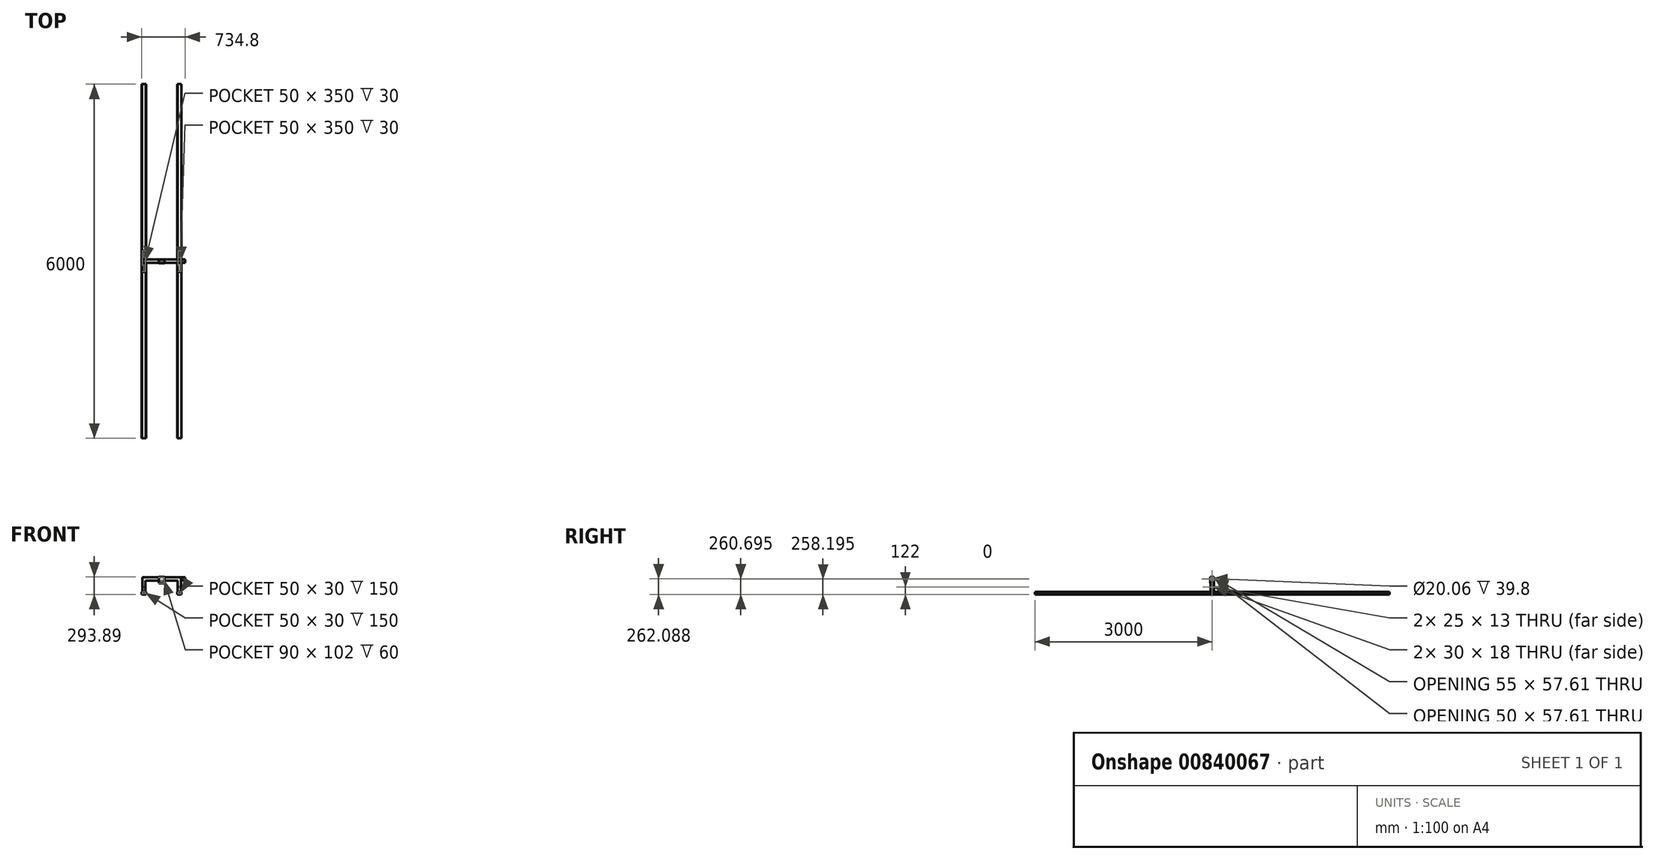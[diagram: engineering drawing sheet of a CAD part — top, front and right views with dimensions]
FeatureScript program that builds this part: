
annotation { "Feature Type Name" : "Feature", "Feature Type Description" : "" }
export const myFeature = defineFeature(function(context is Context, id is Id, definition is map)
    precondition{}
    {
        {
            var Q0;
            Q0=qCreatedBy(makeId("Top.planeOp"),FACE);
            var sketch = newSketch(context, id + "F0", { "sketchPlane" : qUnion([Q0])});
            skLineSegment(sketch, "E0", {"start": v(-300, 0) * mm, "end": v(300, 0) * mm});
            skLineSegment(sketch, "E1.bottom", {"start": v(-275, -25) * mm, "end": v(-325, -25) * mm});
            skLineSegment(sketch, "E1.top", {"start": v(-275, 25) * mm, "end": v(-325, 25) * mm});
            skLineSegment(sketch, "E1.left", {"start": v(-275, -25) * mm, "end": v(-275, 25) * mm});
            skLineSegment(sketch, "E1.right", {"start": v(-325, -25) * mm, "end": v(-325, 25) * mm});
            skPoint(sketch, "E1.middle", {"position": v(-300, 0) * mm});
            skLineSegment(sketch, "E2", {"start": v(0, 0) * mm, "end": v(0, 104.38) * mm, "construction": true});
            skLineSegment(sketch, "E3.MirrorCS", {"start": v(275, 25) * mm, "end": v(325, 25) * mm});
            skLineSegment(sketch, "E4.MirrorCS", {"start": v(275, -25) * mm, "end": v(275, 25) * mm});
            skLineSegment(sketch, "E5.MirrorCS", {"start": v(325, -25) * mm, "end": v(325, 25) * mm});
            skLineSegment(sketch, "E6.MirrorCS", {"start": v(275, -25) * mm, "end": v(325, -25) * mm});
            skSolve(sketch);
        }
        {
            var Q0;
            Q0 = qSketchRegion(id + "F0", true);
            extrude(context, id + "F1", {"entities" : qUnion([Q0]), "endBound" : BoundingType.SYMMETRIC, "depth" : 220 * mm, "offsetDistance" : 25 * mm});
        }
        {
            var Q0;
            Q0=makeQuery(id+"F1.opExtrude","CAP_FACE",FACE,{"disambiguationData":[OSD([sQuery(id+"F0.wireOp",EDGE,"E1.bottom"),sQuery(id+"F0.wireOp",EDGE,"E1.top"),sQuery(id+"F0.wireOp",EDGE,"E1.left"),sQuery(id+"F0.wireOp",EDGE,"E1.right")])],"isStart":false});
            var sketch = newSketch(context, id + "F2", { "sketchPlane" : qUnion([Q0])});
            skLineSegment(sketch, "E7.0.1", {"start": v(-275, 25) * mm, "end": v(-325, 25) * mm});
            skLineSegment(sketch, "E7.0.2", {"start": v(-325, 25) * mm, "end": v(-325, -25) * mm});
            skLineSegment(sketch, "E7.0.3", {"start": v(-325, -25) * mm, "end": v(-275, -25) * mm});
            skLineSegment(sketch, "E8.0.1", {"start": v(275, -25) * mm, "end": v(325, -25) * mm});
            skLineSegment(sketch, "E8.0.2", {"start": v(325, -25) * mm, "end": v(325, 25) * mm});
            skLineSegment(sketch, "E8.0.3", {"start": v(325, 25) * mm, "end": v(275, 25) * mm});
            skLineSegment(sketch, "E9", {"start": v(-275, 25) * mm, "end": v(275, 25) * mm});
            skLineSegment(sketch, "E10", {"start": v(-275, -25) * mm, "end": v(275, -25) * mm});
            skSolve(sketch);
        }
        {
            var Q0;
            Q0 = qSketchRegion(id + "F2", true);
            extrude(context, id + "F3", {"entities" : qUnion([Q0]), "operationType" : NewBodyOperationType.ADD, "depth" : 55 * mm, "offsetDistance" : 25 * mm});
        }
        {
            var Q0;
            Q0=makeQuery(id+"F1.opExtrude","SWEPT_FACE",FACE,{"disambiguationData":[OSD([sQuery(id+"F0.wireOp",EDGE,"E1.right")])]});
            var sketch = newSketch(context, id + "F4", { "sketchPlane" : qUnion([Q0])});
            skLineSegment(sketch, "E11.0.0", {"start": v(-25, -110) * mm, "end": v(25, -110) * mm});
            skLineSegment(sketch, "E11.0.1", {"start": v(25, -110) * mm, "end": v(25, 110) * mm});
            skLineSegment(sketch, "E11.0.3", {"start": v(-25, 110) * mm, "end": v(-25, -110) * mm});
            skLineSegment(sketch, "E12", {"start": v(0, 22) * mm, "end": v(0, 9) * mm});
            skLineSegment(sketch, "E13", {"start": v(0, -22) * mm, "end": v(0, -35) * mm});
            skLineSegment(sketch, "E14.bottom", {"start": v(15, 35) * mm, "end": v(-15, 35) * mm});
            skLineSegment(sketch, "E14.top", {"start": v(15, 53) * mm, "end": v(-15, 53) * mm});
            skLineSegment(sketch, "E14.left", {"start": v(15, 35) * mm, "end": v(15, 53) * mm});
            skLineSegment(sketch, "E14.right", {"start": v(-15, 35) * mm, "end": v(-15, 53) * mm});
            skPoint(sketch, "E14.middle", {"position": v(0, 44) * mm});
            skLineSegment(sketch, "E15.bottom", {"start": v(15, -9) * mm, "end": v(-15, -9) * mm});
            skLineSegment(sketch, "E15.top", {"start": v(15, 9) * mm, "end": v(-15, 9) * mm});
            skLineSegment(sketch, "E15.left", {"start": v(15, -9) * mm, "end": v(15, 9) * mm});
            skLineSegment(sketch, "E15.right", {"start": v(-15, -9) * mm, "end": v(-15, 9) * mm});
            skLineSegment(sketch, "E16.bottom", {"start": v(15, -53) * mm, "end": v(-15, -53) * mm});
            skLineSegment(sketch, "E16.top", {"start": v(15, -35) * mm, "end": v(-15, -35) * mm});
            skLineSegment(sketch, "E16.left", {"start": v(15, -53) * mm, "end": v(15, -35) * mm});
            skLineSegment(sketch, "E16.right", {"start": v(-15, -53) * mm, "end": v(-15, -35) * mm});
            skPoint(sketch, "E16.middle", {"position": v(0, -44) * mm});
            skPoint(sketch, "E17.trimOffspring.end.orphan", {"position": v(0, -110) * mm});
            skLineSegment(sketch, "E18.trimOffspring", {"start": v(0, -53) * mm, "end": v(0, -66) * mm});
            skLineSegment(sketch, "E19.trimOffspring", {"start": v(0, -9) * mm, "end": v(0, -22) * mm});
            skLineSegment(sketch, "E20.trimOffspring", {"start": v(0, -9) * mm, "end": v(0, -35) * mm});
            skLineSegment(sketch, "E21.trimOffspring", {"start": v(0, 35) * mm, "end": v(0, 22) * mm});
            skLineSegment(sketch, "E22.trimOffspring", {"start": v(0, 35) * mm, "end": v(0, 9) * mm});
            skLineSegment(sketch, "E23.0.1", {"start": v(25, -110) * mm, "end": v(25, 165) * mm});
            skLineSegment(sketch, "E23.0.2", {"start": v(25, 165) * mm, "end": v(-25, 165) * mm});
            skLineSegment(sketch, "E23.0.3", {"start": v(-25, 165) * mm, "end": v(-25, -110) * mm});
            skSolve(sketch);
        }
        {
            var Q0;
            {var subQ3=sQuery(id+"F4.wireOp",EDGE,"E15.left");Q0=makeQuery(id+"F4.imprint","IMPRINT",FACE,{"disambiguationData":[TD([[makeQuery(id+"F4.imprint","IMPRINT",EDGE,{"derivedFrom":subQ3}),1.0]])]});}
            extrude(context, id + "F5", {"entities" : qUnion([Q0]), "operationType" : NewBodyOperationType.REMOVE, "oppositeDirection" : true, "depth" : 696 * mm, "offsetDistance" : 25 * mm});
        }
        {
            var Q0;
            Q0=makeQuery(id+"F3.opExtrude","CAP_FACE",FACE,{"disambiguationData":[OSD([sQuery(id+"F2.wireOp",EDGE,"E7.0.1"),sQuery(id+"F2.wireOp",EDGE,"E7.0.2"),sQuery(id+"F2.wireOp",EDGE,"E7.0.3"),sQuery(id+"F2.wireOp",EDGE,"E8.0.1"),sQuery(id+"F2.wireOp",EDGE,"E8.0.2"),sQuery(id+"F2.wireOp",EDGE,"E8.0.3"),sQuery(id+"F2.wireOp",EDGE,"E9"),sQuery(id+"F2.wireOp",EDGE,"E10")])],"isStart":false});
            var sketch = newSketch(context, id + "F6", { "sketchPlane" : qUnion([Q0])});
            skPoint(sketch, "E24.orphan", {"position": v(-292.5, -12.5) * mm});
            skPoint(sketch, "E25.orphan", {"position": v(-247.5, 12.5) * mm});
            skPoint(sketch, "E26.left.start.orphan", {"position": v(-240.34, -12.5) * mm});
            skPoint(sketch, "E26.right.end.orphan", {"position": v(-292.5, 12.5) * mm});
            skPoint(sketch, "E27.bottom.end.orphan", {"position": v(-182.5, -12.5) * mm});
            skPoint(sketch, "E28.orphan", {"position": v(-130.34, -12.5) * mm});
            skPoint(sketch, "E27.top.end.orphan", {"position": v(-182.5, 12.5) * mm});
            skPoint(sketch, "E27.top.start.orphan", {"position": v(-137.5, 12.5) * mm});
            skPoint(sketch, "E29.top.end.orphan", {"position": v(37.5, 12.5) * mm});
            skPoint(sketch, "E29.bottom.end.orphan", {"position": v(37.5, -12.5) * mm});
            skPoint(sketch, "E30.orphan", {"position": v(82.5, -12.5) * mm});
            skPoint(sketch, "E29.left.end.orphan", {"position": v(82.5, 12.5) * mm});
            skPoint(sketch, "E31.top.end.orphan", {"position": v(197.5, 12.5) * mm});
            skPoint(sketch, "E31.bottom.end.orphan", {"position": v(197.5, -12.5) * mm});
            skPoint(sketch, "E31.bottom.start.orphan", {"position": v(242.5, -12.5) * mm});
            skPoint(sketch, "E31.left.end.orphan", {"position": v(242.5, 12.5) * mm});
            skPoint(sketch, "E32.orphan", {"position": v(-72.5, -12.5) * mm});
            skPoint(sketch, "E33.orphan", {"position": v(-27.5, -12.5) * mm});
            skPoint(sketch, "E34.top.end.orphan", {"position": v(-72.5, 12.5) * mm});
            skPoint(sketch, "E34.top.start.orphan", {"position": v(-27.5, 12.5) * mm});
            skPoint(sketch, "E35.orphan", {"position": v(325, 0) * mm});
            skPoint(sketch, "E36.orphan", {"position": v(-325, 0) * mm});
            skLineSegment(sketch, "E37", {"start": v(-325, 0) * mm, "end": v(325, 0) * mm, "construction": true});
            skLineSegment(sketch, "E38", {"start": v(-325, 0) * mm, "end": v(-195, 0) * mm});
            skLineSegment(sketch, "E39", {"start": v(-195, 0) * mm, "end": v(-65, 0) * mm});
            skLineSegment(sketch, "E40", {"start": v(-65, 0) * mm, "end": v(65, 0) * mm});
            skLineSegment(sketch, "E41", {"start": v(65, 0) * mm, "end": v(195, 0) * mm});
            skLineSegment(sketch, "E42", {"start": v(195, 0) * mm, "end": v(325, 0) * mm});
            skLineSegment(sketch, "E43.top", {"start": v(-242.5, 12.5) * mm, "end": v(-247.5, 12.5) * mm});
            skPoint(sketch, "E43.middle", {"position": v(-260, 0) * mm});
            skPoint(sketch, "E44.orphan", {"position": v(-277.5, -12.5) * mm});
            skPoint(sketch, "E43.left.start.orphan", {"position": v(-242.5, -12.5) * mm});
            skPoint(sketch, "E45.orphan", {"position": v(-277.5, 12.5) * mm});
            skLineSegment(sketch, "E46.bottom", {"start": v(22.5, -12.5) * mm, "end": v(-22.5, -12.5) * mm});
            skLineSegment(sketch, "E46.top", {"start": v(22.5, 12.5) * mm, "end": v(-22.5, 12.5) * mm});
            skLineSegment(sketch, "E46.left", {"start": v(22.5, -12.5) * mm, "end": v(22.5, 12.5) * mm});
            skLineSegment(sketch, "E46.right", {"start": v(-22.5, -12.5) * mm, "end": v(-22.5, 12.5) * mm});
            skPoint(sketch, "E46.middle", {"position": v(0, 0) * mm});
            skLineSegment(sketch, "E47", {"start": v(0, 0) * mm, "end": v(-65, 0) * mm});
            skLineSegment(sketch, "E48", {"start": v(0, 0) * mm, "end": v(-110, 0) * mm});
            skLineSegment(sketch, "E49.bottom", {"start": v(-87.5, -12.5) * mm, "end": v(-132.5, -12.5) * mm});
            skLineSegment(sketch, "E49.top", {"start": v(-87.5, 12.5) * mm, "end": v(-132.5, 12.5) * mm});
            skLineSegment(sketch, "E49.left", {"start": v(-87.5, -12.5) * mm, "end": v(-87.5, 12.5) * mm});
            skLineSegment(sketch, "E49.right", {"start": v(-132.5, -12.5) * mm, "end": v(-132.5, 12.5) * mm});
            skPoint(sketch, "E49.middle", {"position": v(-110, 0) * mm});
            skLineSegment(sketch, "E50", {"start": v(0, 0) * mm, "end": v(110, 0) * mm});
            skLineSegment(sketch, "E51.bottom", {"start": v(132.5, -12.5) * mm, "end": v(87.5, -12.5) * mm});
            skLineSegment(sketch, "E51.top", {"start": v(132.5, 12.5) * mm, "end": v(87.5, 12.5) * mm});
            skLineSegment(sketch, "E51.left", {"start": v(132.5, -12.5) * mm, "end": v(132.5, 12.5) * mm});
            skLineSegment(sketch, "E51.right", {"start": v(87.5, -12.5) * mm, "end": v(87.5, 12.5) * mm});
            skPoint(sketch, "E51.middle", {"position": v(110, 0) * mm});
            skLineSegment(sketch, "E52", {"start": v(-110, 0) * mm, "end": v(-220, 0) * mm});
            skLineSegment(sketch, "E53.bottom", {"start": v(-197.5, -12.5) * mm, "end": v(-242.5, -12.5) * mm});
            skLineSegment(sketch, "E53.top", {"start": v(-197.5, 12.5) * mm, "end": v(-242.5, 12.5) * mm});
            skLineSegment(sketch, "E53.left", {"start": v(-197.5, -12.5) * mm, "end": v(-197.5, 12.5) * mm});
            skLineSegment(sketch, "E53.right", {"start": v(-242.5, -12.5) * mm, "end": v(-242.5, 12.5) * mm});
            skPoint(sketch, "E53.middle", {"position": v(-220, 0) * mm});
            skLineSegment(sketch, "E54", {"start": v(110, 0) * mm, "end": v(220, 0) * mm});
            skPoint(sketch, "E55.middle", {"position": v(195, 0) * mm});
            skPoint(sketch, "E56.orphan", {"position": v(172.5, -12.5) * mm});
            skPoint(sketch, "E57.orphan", {"position": v(172.5, 12.5) * mm});
            skPoint(sketch, "E58.orphan", {"position": v(217.5, 12.5) * mm});
            skPoint(sketch, "E55.bottom.start.orphan", {"position": v(217.5, -12.5) * mm});
            skLineSegment(sketch, "E59.bottom", {"start": v(242.5, -12.5) * mm, "end": v(197.5, -12.5) * mm});
            skLineSegment(sketch, "E59.top", {"start": v(242.5, 12.5) * mm, "end": v(197.5, 12.5) * mm});
            skLineSegment(sketch, "E59.left", {"start": v(242.5, -12.5) * mm, "end": v(242.5, 12.5) * mm});
            skLineSegment(sketch, "E59.right", {"start": v(197.5, -12.5) * mm, "end": v(197.5, 12.5) * mm});
            skPoint(sketch, "E59.middle", {"position": v(220, 0) * mm});
            skSolve(sketch);
        }
        {
            var Q0;
            Q0=makeQuery(id+"F3.boolean.opBoolean","MERGE",FACE,{"derivedFrom":[makeQuery(id+"F1.opExtrude","SWEPT_FACE",FACE,{"disambiguationData":[OSD([sQuery(id+"F0.wireOp",EDGE,"E1.bottom")])]}),makeQuery(id+"F1.opExtrude","SWEPT_FACE",FACE,{"disambiguationData":[OSD([sQuery(id+"F0.wireOp",EDGE,"E6.MirrorCS")])]}),makeQuery(id+"F3.opExtrude","SWEPT_FACE",FACE,{"disambiguationData":[OSD([sQuery(id+"F2.wireOp",EDGE,"E7.0.3"),sQuery(id+"F2.wireOp",EDGE,"E8.0.1"),sQuery(id+"F2.wireOp",EDGE,"E10")])]})]});
            var sketch = newSketch(context, id + "F7", { "sketchPlane" : qUnion([Q0])});
            skLineSegment(sketch, "E60.bottom", {"start": v(-325, -110) * mm, "end": v(-275, -110) * mm});
            skLineSegment(sketch, "E60.top", {"start": v(-325, -80) * mm, "end": v(-275, -80) * mm});
            skLineSegment(sketch, "E60.left", {"start": v(-325, -110) * mm, "end": v(-325, -80) * mm});
            skLineSegment(sketch, "E60.right", {"start": v(-275, -110) * mm, "end": v(-275, -80) * mm});
            skLineSegment(sketch, "E61", {"start": v(0, 0) * mm, "end": v(0, 200.3) * mm, "construction": true});
            skLineSegment(sketch, "E62.MirrorCS", {"start": v(325, -80) * mm, "end": v(275, -80) * mm});
            skLineSegment(sketch, "E63.MirrorCS", {"start": v(275, -110) * mm, "end": v(275, -80) * mm});
            skLineSegment(sketch, "E64.MirrorCS", {"start": v(325, -110) * mm, "end": v(275, -110) * mm});
            skLineSegment(sketch, "E65.MirrorCS", {"start": v(325, -110) * mm, "end": v(325, -80) * mm});
            skSolve(sketch);
        }
        {
            var Q0;
            Q0 = qSketchRegion(id + "F7", true);
            extrude(context, id + "F8", {"entities" : qUnion([Q0]), "operationType" : NewBodyOperationType.ADD, "depth" : 150 * mm, "offsetDistance" : 25 * mm});
        }
        {
            var Q0;
            Q0=makeQuery(id+"F3.boolean.opBoolean","MERGE",FACE,{"derivedFrom":[makeQuery(id+"F1.opExtrude","SWEPT_FACE",FACE,{"disambiguationData":[OSD([sQuery(id+"F0.wireOp",EDGE,"E1.top")])]}),makeQuery(id+"F1.opExtrude","SWEPT_FACE",FACE,{"disambiguationData":[OSD([sQuery(id+"F0.wireOp",EDGE,"E3.MirrorCS")])]}),makeQuery(id+"F3.opExtrude","SWEPT_FACE",FACE,{"disambiguationData":[OSD([sQuery(id+"F2.wireOp",EDGE,"E7.0.1"),sQuery(id+"F2.wireOp",EDGE,"E8.0.3"),sQuery(id+"F2.wireOp",EDGE,"E9")])]})]});
            var sketch = newSketch(context, id + "F9", { "sketchPlane" : qUnion([Q0])});
            skLineSegment(sketch, "E66.bottom", {"start": v(-325, -110) * mm, "end": v(-275, -110) * mm});
            skLineSegment(sketch, "E66.top", {"start": v(-325, -80) * mm, "end": v(-275, -80) * mm});
            skLineSegment(sketch, "E66.left", {"start": v(-325, -110) * mm, "end": v(-325, -80) * mm});
            skLineSegment(sketch, "E66.right", {"start": v(-275, -110) * mm, "end": v(-275, -80) * mm});
            skLineSegment(sketch, "E67", {"start": v(0, 0) * mm, "end": v(0, 248.63) * mm, "construction": true});
            skLineSegment(sketch, "E68.MirrorCS", {"start": v(325, -80) * mm, "end": v(275, -80) * mm});
            skLineSegment(sketch, "E69.MirrorCS", {"start": v(325, -110) * mm, "end": v(275, -110) * mm});
            skLineSegment(sketch, "E70.MirrorCS", {"start": v(275, -110) * mm, "end": v(275, -80) * mm});
            skLineSegment(sketch, "E71.MirrorCS", {"start": v(325, -110) * mm, "end": v(325, -80) * mm});
            skSolve(sketch);
        }
        {
            var Q0;
            Q0 = qSketchRegion(id + "F9", true);
            extrude(context, id + "F10", {"entities" : qUnion([Q0]), "operationType" : NewBodyOperationType.ADD, "depth" : 150 * mm, "offsetDistance" : 25 * mm});
        }
        {
            var Q0;
            Q0=qCreatedBy(makeId("Front.planeOp"),FACE);
            var sketch = newSketch(context, id + "F11", { "sketchPlane" : qUnion([Q0])});
            skLineSegment(sketch, "E72.0", {"start": v(-275, -117) * mm, "end": v(-325, -117) * mm});
            skLineSegment(sketch, "E73.0", {"start": v(-268, -80) * mm, "end": v(-268, -110) * mm});
            skLineSegment(sketch, "E74.0", {"start": v(-332, -80) * mm, "end": v(-332, -110) * mm});
            skLineSegment(sketch, "E75", {"start": v(-332, -110) * mm, "end": v(-332, -117) * mm});
            skLineSegment(sketch, "E76", {"start": v(-332, -117) * mm, "end": v(-325, -117) * mm});
            skLineSegment(sketch, "E77", {"start": v(-268, -117) * mm, "end": v(-268, -110) * mm});
            skLineSegment(sketch, "E78", {"start": v(-268, -117) * mm, "end": v(-275, -117) * mm});
            skLineSegment(sketch, "E79.0", {"start": v(-337, -80) * mm, "end": v(-337, -110) * mm});
            skLineSegment(sketch, "E79.1", {"start": v(-337, -110) * mm, "end": v(-337, -122) * mm});
            skLineSegment(sketch, "E79.2", {"start": v(-337, -122) * mm, "end": v(-325, -122) * mm});
            skLineSegment(sketch, "E79.3", {"start": v(-263, -80) * mm, "end": v(-263, -110) * mm});
            skLineSegment(sketch, "E79.4", {"start": v(-263, -122) * mm, "end": v(-263, -110) * mm});
            skLineSegment(sketch, "E79.5", {"start": v(-263, -122) * mm, "end": v(-275, -122) * mm});
            skLineSegment(sketch, "E79.6", {"start": v(-275, -122) * mm, "end": v(-325, -122) * mm});
            skLineSegment(sketch, "E80", {"start": v(-332, -80) * mm, "end": v(-337, -80) * mm});
            skLineSegment(sketch, "E81", {"start": v(-268, -80) * mm, "end": v(-263, -80) * mm});
            skLineSegment(sketch, "E82", {"start": v(0, 0) * mm, "end": v(0, 202.62) * mm, "construction": true});
            skLineSegment(sketch, "E83.MirrorCS", {"start": v(263, -80) * mm, "end": v(263, -110) * mm});
            skLineSegment(sketch, "E84.MirrorCS", {"start": v(275, -122) * mm, "end": v(325, -122) * mm});
            skLineSegment(sketch, "E85.MirrorCS", {"start": v(275, -117) * mm, "end": v(325, -117) * mm});
            skLineSegment(sketch, "E86.MirrorCS", {"start": v(337, -80) * mm, "end": v(337, -110) * mm});
            skLineSegment(sketch, "E87.MirrorCS", {"start": v(332, -80) * mm, "end": v(332, -110) * mm});
            skLineSegment(sketch, "E88.MirrorCS", {"start": v(332, -80) * mm, "end": v(337, -80) * mm});
            skLineSegment(sketch, "E89.MirrorCS", {"start": v(332, -110) * mm, "end": v(332, -117) * mm});
            skLineSegment(sketch, "E90.MirrorCS", {"start": v(332, -117) * mm, "end": v(325, -117) * mm});
            skLineSegment(sketch, "E91.MirrorCS", {"start": v(268, -117) * mm, "end": v(268, -110) * mm});
            skLineSegment(sketch, "E92.MirrorCS", {"start": v(268, -117) * mm, "end": v(275, -117) * mm});
            skLineSegment(sketch, "E93.MirrorCS", {"start": v(268, -80) * mm, "end": v(268, -110) * mm});
            skLineSegment(sketch, "E94.MirrorCS", {"start": v(268, -80) * mm, "end": v(263, -80) * mm});
            skLineSegment(sketch, "E95.MirrorCS", {"start": v(263, -122) * mm, "end": v(263, -110) * mm});
            skLineSegment(sketch, "E96.MirrorCS", {"start": v(263, -122) * mm, "end": v(275, -122) * mm});
            skLineSegment(sketch, "E97", {"start": v(337, -110) * mm, "end": v(337, -122) * mm});
            skLineSegment(sketch, "E98", {"start": v(337, -122) * mm, "end": v(325, -122) * mm});
            skSolve(sketch);
        }
        {
            var Q0;
            Q0 = qSketchRegion(id + "F11", true);
            extrude(context, id + "F12", {"entities" : qUnion([Q0]), "endBound" : BoundingType.SYMMETRIC, "depth" : 6000 * mm, "offsetDistance" : 25 * mm});
        }
        {
            var Q0;
            Q0=qCreatedBy(makeId("Right.planeOp"),FACE);
            var sketch = newSketch(context, id + "F13", { "sketchPlane" : qUnion([Q0])});
            skLineSegment(sketch, "E99.0.3", {"start": v(-25, 127.87) * mm, "end": v(-25, 165) * mm});
            skLineSegment(sketch, "E99.0.4", {"start": v(-25, 165) * mm, "end": v(25, 165) * mm});
            skLineSegment(sketch, "E99.0.5", {"start": v(25, 165) * mm, "end": v(25, 127.87) * mm});
            skLineSegment(sketch, "E100.left", {"start": v(-25, 165) * mm, "end": v(-25, 127.87) * mm});
            skLineSegment(sketch, "E101", {"start": v(25, 127.87) * mm, "end": v(25, 107.4) * mm});
            skLineSegment(sketch, "E102", {"start": v(25, 102.4) * mm, "end": v(-25, 102.4) * mm});
            skLineSegment(sketch, "E103", {"start": v(-25, 107.4) * mm, "end": v(-25, 127.87) * mm});
            skLineSegment(sketch, "E104", {"start": v(-25, 102.4) * mm, "end": v(-30, 102.4) * mm});
            skLineSegment(sketch, "E105", {"start": v(-30, 102.4) * mm, "end": v(-30, 169.4) * mm});
            skLineSegment(sketch, "E106", {"start": v(-30, 169.4) * mm, "end": v(30, 169.4) * mm});
            skLineSegment(sketch, "E107", {"start": v(30, 169.4) * mm, "end": v(30, 102.4) * mm});
            skLineSegment(sketch, "E108", {"start": v(30, 102.4) * mm, "end": v(25, 102.4) * mm});
            skLineSegment(sketch, "E109", {"start": v(25, 107.4) * mm, "end": v(-25, 107.4) * mm});
            skPoint(sketch, "E110.orphan", {"position": v(30, 107.4) * mm});
            skSolve(sketch);
        }
        {
            var Q0;
            Q0 = qSketchRegion(id + "F13", true);
            extrude(context, id + "F14", {"entities" : qUnion([Q0]), "operationType" : NewBodyOperationType.ADD, "endBound" : BoundingType.SYMMETRIC, "depth" : 90 * mm, "offsetDistance" : 25 * mm});
        }
        {
            var Q0;
            Q0=makeQuery(id+"F14.opExtrude","SWEPT_FACE",FACE,{"disambiguationData":[OSD([sQuery(id+"F13.wireOp",EDGE,"E102"),sQuery(id+"F13.wireOp",EDGE,"E104"),sQuery(id+"F13.wireOp",EDGE,"E108")])]});
            var sketch = newSketch(context, id + "F15", { "sketchPlane" : qUnion([Q0])});
            skLineSegment(sketch, "E111.0.0", {"start": v(-45, 30) * mm, "end": v(-45, -30) * mm});
            skLineSegment(sketch, "E111.0.1", {"start": v(-45, -30) * mm, "end": v(45, -30) * mm});
            skLineSegment(sketch, "E111.0.2", {"start": v(45, -30) * mm, "end": v(45, 30) * mm});
            skLineSegment(sketch, "E111.0.3", {"start": v(45, 30) * mm, "end": v(-45, 30) * mm});
            skLineSegment(sketch, "E112.bottom", {"start": v(22.5, -12.5) * mm, "end": v(-22.5, -12.5) * mm});
            skLineSegment(sketch, "E112.top", {"start": v(22.5, 12.5) * mm, "end": v(-22.5, 12.5) * mm});
            skLineSegment(sketch, "E112.left", {"start": v(22.5, -12.5) * mm, "end": v(22.5, 12.5) * mm});
            skLineSegment(sketch, "E112.right", {"start": v(-22.5, -12.5) * mm, "end": v(-22.5, 12.5) * mm});
            skPoint(sketch, "E112.middle", {"position": v(0, 0) * mm});
            skSolve(sketch);
        }
        {
            var Q0;
            Q0 = qSketchRegion(id + "F15", true);
            extrude(context, id + "F16", {"entities" : qUnion([Q0]), "operationType" : NewBodyOperationType.ADD, "depth" : 35 * mm, "offsetDistance" : 25 * mm});
        }
        {
            var Q0;
            Q0=makeQuery(id+"F10.boolean.opBoolean","MERGE",FACE,{"derivedFrom":[makeQuery(id+"F8.boolean.opBoolean","MERGE",FACE,{"derivedFrom":[makeQuery(id+"F3.boolean.opBoolean","MERGE",FACE,{"derivedFrom":[makeQuery(id+"F1.opExtrude","SWEPT_FACE",FACE,{"disambiguationData":[OSD([sQuery(id+"F0.wireOp",EDGE,"E1.right")])]}),makeQuery(id+"F3.opExtrude","SWEPT_FACE",FACE,{"disambiguationData":[OSD([sQuery(id+"F2.wireOp",EDGE,"E7.0.2")])]})]}),makeQuery(id+"F8.opExtrude","SWEPT_FACE",FACE,{"disambiguationData":[OSD([sQuery(id+"F7.wireOp",EDGE,"E60.left")])]})]}),makeQuery(id+"F10.opExtrude","SWEPT_FACE",FACE,{"disambiguationData":[OSD([sQuery(id+"F9.wireOp",EDGE,"E71.MirrorCS")])]})]});
            var sketch = newSketch(context, id + "F17", { "sketchPlane" : qUnion([Q0])});
            skLineSegment(sketch, "E113.0.4", {"start": v(25, 165) * mm, "end": v(-25, 165) * mm});
            skLineSegment(sketch, "E113.0.5", {"start": v(-25, 165) * mm, "end": v(-25, 115) * mm});
            skLineSegment(sketch, "E114", {"start": v(-25, 115) * mm, "end": v(25, 115) * mm});
            skLineSegment(sketch, "E115", {"start": v(25, 115) * mm, "end": v(25, 165) * mm});
            skPoint(sketch, "E113.0.7.end.orphan", {"position": v(-175, -110) * mm});
            skPoint(sketch, "E113.0.6.end.orphan", {"position": v(-175, -80) * mm});
            skPoint(sketch, "E113.0.6.start.orphan", {"position": v(-25, -80) * mm});
            skPoint(sketch, "E113.0.2.end.orphan", {"position": v(25, -80) * mm});
            skPoint(sketch, "E113.0.1.end.orphan", {"position": v(175, -80) * mm});
            skPoint(sketch, "E113.0.1.start.orphan", {"position": v(175, -110) * mm});
            skLineSegment(sketch, "E116", {"start": v(-25, 140) * mm, "end": v(25, 140) * mm, "construction": true});
            skCircle(sketch, "E117", {"center": v(0, 140) * mm, "radius": 10 * mm});
            skSolve(sketch);
        }
        {
            var Q0;
            Q0=makeQuery(id+"F3.opExtrude","CAP_FACE",FACE,{"disambiguationData":[OSD([sQuery(id+"F2.wireOp",EDGE,"E7.0.1"),sQuery(id+"F2.wireOp",EDGE,"E7.0.2"),sQuery(id+"F2.wireOp",EDGE,"E7.0.3"),sQuery(id+"F2.wireOp",EDGE,"E8.0.1"),sQuery(id+"F2.wireOp",EDGE,"E8.0.2"),sQuery(id+"F2.wireOp",EDGE,"E8.0.3"),sQuery(id+"F2.wireOp",EDGE,"E9"),sQuery(id+"F2.wireOp",EDGE,"E10")])],"isStart":true});
            shell(context, id + "F18", {"entities" : qUnion([Q0]), "thickness" : 2.5 * mm, "oppositeDirection" : true});
        }
        {
            var Q0;
            Q0=sQuery(id+"F17.wireOp",EDGE,"E117");
            extrude(context, id + "F19", {"bodyType" : ToolBodyType.SURFACE, "surfaceEntities" : qUnion([Q0]), "oppositeDirection" : true, "depth" : 692 * mm, "offsetDistance" : 25 * mm});
        }
        {
            var Q0;
            Q0=sQuery(id+"F17.wireOp",EDGE,"E117");
            extrude(context, id + "F20", {"bodyType" : ToolBodyType.SURFACE, "surfaceOperationType" : NewSurfaceOperationType.ADD, "surfaceEntities" : qUnion([Q0]), "depth" : 60 * mm, "offsetDistance" : 25 * mm});
        }
        {
            var Q0;
            Q0=makeQuery(id+"F10.boolean.opBoolean","MERGE",FACE,{"derivedFrom":[makeQuery(id+"F8.boolean.opBoolean","MERGE",FACE,{"derivedFrom":[makeQuery(id+"F3.boolean.opBoolean","MERGE",FACE,{"derivedFrom":[makeQuery(id+"F1.opExtrude","SWEPT_FACE",FACE,{"disambiguationData":[OSD([sQuery(id+"F0.wireOp",EDGE,"E5.MirrorCS")])]}),makeQuery(id+"F3.opExtrude","SWEPT_FACE",FACE,{"disambiguationData":[OSD([sQuery(id+"F2.wireOp",EDGE,"E8.0.2")])]})]}),makeQuery(id+"F8.opExtrude","SWEPT_FACE",FACE,{"disambiguationData":[OSD([sQuery(id+"F7.wireOp",EDGE,"E65.MirrorCS")])]})]}),makeQuery(id+"F10.opExtrude","SWEPT_FACE",FACE,{"disambiguationData":[OSD([sQuery(id+"F9.wireOp",EDGE,"E66.left")])]})]});
            var sketch = newSketch(context, id + "F21", { "sketchPlane" : qUnion([Q0])});
            skLineSegment(sketch, "E118.0.3", {"start": v(27.5, 115.21) * mm, "end": v(27.5, 167.5) * mm});
            skLineSegment(sketch, "E118.0.4", {"start": v(27.5, 167.5) * mm, "end": v(-27.5, 167.5) * mm});
            skLineSegment(sketch, "E118.0.5", {"start": v(-27.5, 167.5) * mm, "end": v(-27.5, 115.21) * mm});
            skLineSegment(sketch, "E119", {"start": v(-24.77, 115.21) * mm, "end": v(25.12, 115.21) * mm});
            skLineSegment(sketch, "E120", {"start": v(25.12, 115.21) * mm, "end": v(27.5, 115.21) * mm});
            skLineSegment(sketch, "E121", {"start": v(27.5, 115.21) * mm, "end": v(-27.5, 115.21) * mm});
            skPoint(sketch, "E118.0.2.end.orphan", {"position": v(27.5, -77.5) * mm});
            skPoint(sketch, "E118.0.1.end.orphan", {"position": v(177.5, -77.5) * mm});
            skPoint(sketch, "E118.0.6.start.orphan", {"position": v(-27.5, -77.5) * mm});
            skPoint(sketch, "E118.0.7.start.orphan", {"position": v(-177.5, -77.5) * mm});
            skPoint(sketch, "E118.0.0.end.orphan", {"position": v(177.5, -112.5) * mm});
            skPoint(sketch, "E118.0.0.start.orphan", {"position": v(-177.5, -112.5) * mm});
            skPoint(sketch, "E122.end.orphan", {"position": v(0, 167.5) * mm});
            skPoint(sketch, "E123.end.orphan", {"position": v(0, 141.36) * mm});
            skPoint(sketch, "E124.orphan", {"position": v(27.5, 141.36) * mm});
            skPoint(sketch, "E125.start.orphan", {"position": v(-27.5, 141.36) * mm});
            skLineSegment(sketch, "E126", {"start": v(0, 141.36) * mm, "end": v(0, 140.09) * mm});
            skCircle(sketch, "E127", {"center": v(0, 140.09) * mm, "radius": 10.03 * mm});
            skSolve(sketch);
        }
        {
            var Q0;
            Q0 = qSketchRegion(id + "F21", true);
            extrude(context, id + "F22", {"entities" : qUnion([Q0]), "depth" : 70.3 * mm, "offsetDistance" : 25 * mm});
        }
        {
            var Q0;
            Q0=makeQuery(id+"F22.opExtrude","CAP_FACE",FACE,{"disambiguationData":[OSD([sQuery(id+"F21.wireOp",EDGE,"E118.0.3"),sQuery(id+"F21.wireOp",EDGE,"E118.0.4"),sQuery(id+"F21.wireOp",EDGE,"E118.0.5"),sQuery(id+"F21.wireOp",EDGE,"E121"),sQuery(id+"F21.wireOp",EDGE,"E127")])],"isStart":false});
            var sketch = newSketch(context, id + "F23", { "sketchPlane" : qUnion([Q0])});
            skCircle(sketch, "E128.0", {"center": v(0, 140.09) * mm, "radius": 10.03 * mm});
            skSolve(sketch);
        }
        {
            var Q0;
            Q0 = qSketchRegion(id + "F23", true);
            extrude(context, id + "F24", {"entities" : qUnion([Q0]), "operationType" : NewBodyOperationType.ADD, "oppositeDirection" : true, "depth" : 30.5 * mm, "offsetDistance" : 25 * mm});
        }
    });
